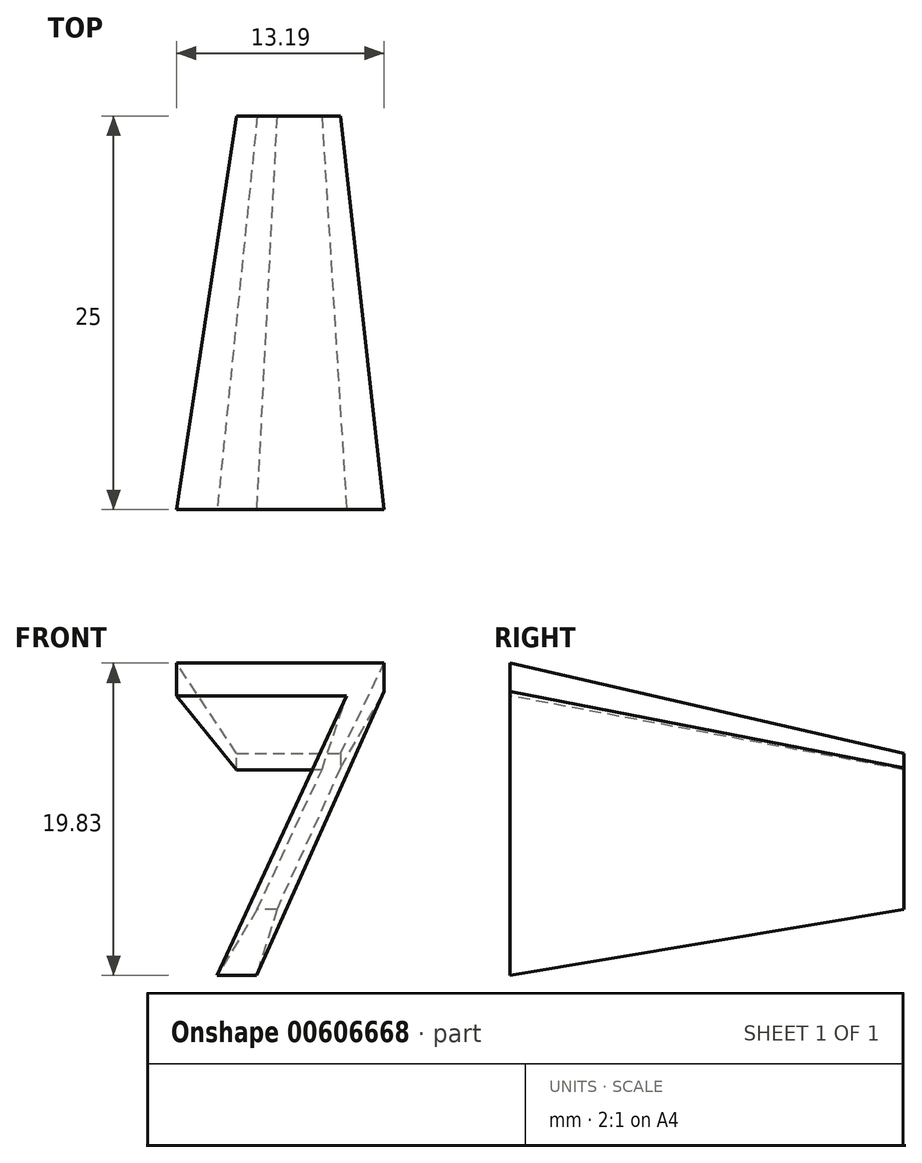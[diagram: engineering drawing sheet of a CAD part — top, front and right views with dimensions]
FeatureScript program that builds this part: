
annotation { "Feature Type Name" : "Feature", "Feature Type Description" : "" }
export const myFeature = defineFeature(function(context is Context, id is Id, definition is map)
    precondition{}
    {
        {
            var Q0;
            Q0=qCreatedBy(makeId("Front.planeOp"),FACE);
            var sketch = newSketch(context, id + "F0", { "sketchPlane" : qUnion([Q0])});
            skText(sketch, "E0", { "text": "7", "fontName": "OpenSans-Regular.ttf"});
            skLineSegment(sketch, "E1.bottom", {"start": v(-3.67, 4.18) * mm, "end": v(4.46, 4.18) * mm});
            skLineSegment(sketch, "E1.top", {"start": v(-3.67, -5.82) * mm, "end": v(4.46, -5.82) * mm});
            skLineSegment(sketch, "E1.left", {"start": v(-3.67, 4.18) * mm, "end": v(-3.67, -5.82) * mm});
            skLineSegment(sketch, "E1.right", {"start": v(4.46, 4.18) * mm, "end": v(4.46, -5.82) * mm});
            const initialGuessF0  = {"E0": [-0.00367, -0.00582, 1, 0, 0.01]};
            skSetInitialGuess(sketch, initialGuessF0);
            skSolve(sketch);
        }
        {
            var Q0;
            {var subQ4=sQuery(id+"F0.wireOp",EDGE,"E0.sketch_text.stroke-0");Q0=makeQuery(id+"F0.imprint","IMPRINT",FACE,{"disambiguationData":[TD([[makeQuery(id+"F0.imprint","IMPRINT",EDGE,{"derivedFrom":subQ4}),1.0]])]});}
            cPlane(context, id + "F1", {"entities" : qUnion([Q0]), "cplaneType" : CPlaneType.OFFSET, "offset" : 25 * mm, "width" : 150 * mm, "height" : 150 * mm});
        }
        {
            var Q0;
            Q0=qCreatedBy(id+"F1.planeOp",FACE);
            var sketch = newSketch(context, id + "F2", { "sketchPlane" : qUnion([Q0])});
            skLineSegment(sketch, "E2.bottom", {"start": v(8.14, -10) * mm, "end": v(-8.14, -10) * mm});
            skLineSegment(sketch, "E2.top", {"start": v(8.14, 10) * mm, "end": v(-8.14, 10) * mm});
            skLineSegment(sketch, "E2.left", {"start": v(8.14, -10) * mm, "end": v(8.14, 10) * mm});
            skLineSegment(sketch, "E2.right", {"start": v(-8.14, -10) * mm, "end": v(-8.14, 10) * mm});
            skPoint(sketch, "E2.middle", {"position": v(0, 0) * mm});
            skText(sketch, "E3", { "text": "7", "fontName": "OpenSans-Regular.ttf"});
            const initialGuessF2  = {"E3": [-0.00814, -0.01, 1, 0, 0.02]};
            skSetInitialGuess(sketch, initialGuessF2);
            skSolve(sketch);
        }
        {
            var Q0;
            {var subQ0=sQuery(id+"F0.wireOp",EDGE,"E0.sketch_text.stroke-0");Q0=makeQuery(id+"F0.imprint","IMPRINT",FACE,{"disambiguationData":[TD([[makeQuery(id+"F0.imprint","IMPRINT",EDGE,{"derivedFrom":subQ0}),-1.0]])]});}
            var Q1;
            Q1=makeQuery(id+"F2.imprint","IMPRINT",FACE,{"disambiguationData":[TD([[makeQuery(id+"F2.imprint","IMPRINT",EDGE,{"derivedFrom":sQuery(id+"F2.wireOp",EDGE,"E3.sketch_text.stroke-0")}),-1.0]])]});
            loft(context, id + "F3", {"sheetProfilesArray" : [{ "sheetProfileEntities" : qUnion([Q0]) }, { "sheetProfileEntities" : qUnion([Q1]) }]});
        }
    });
